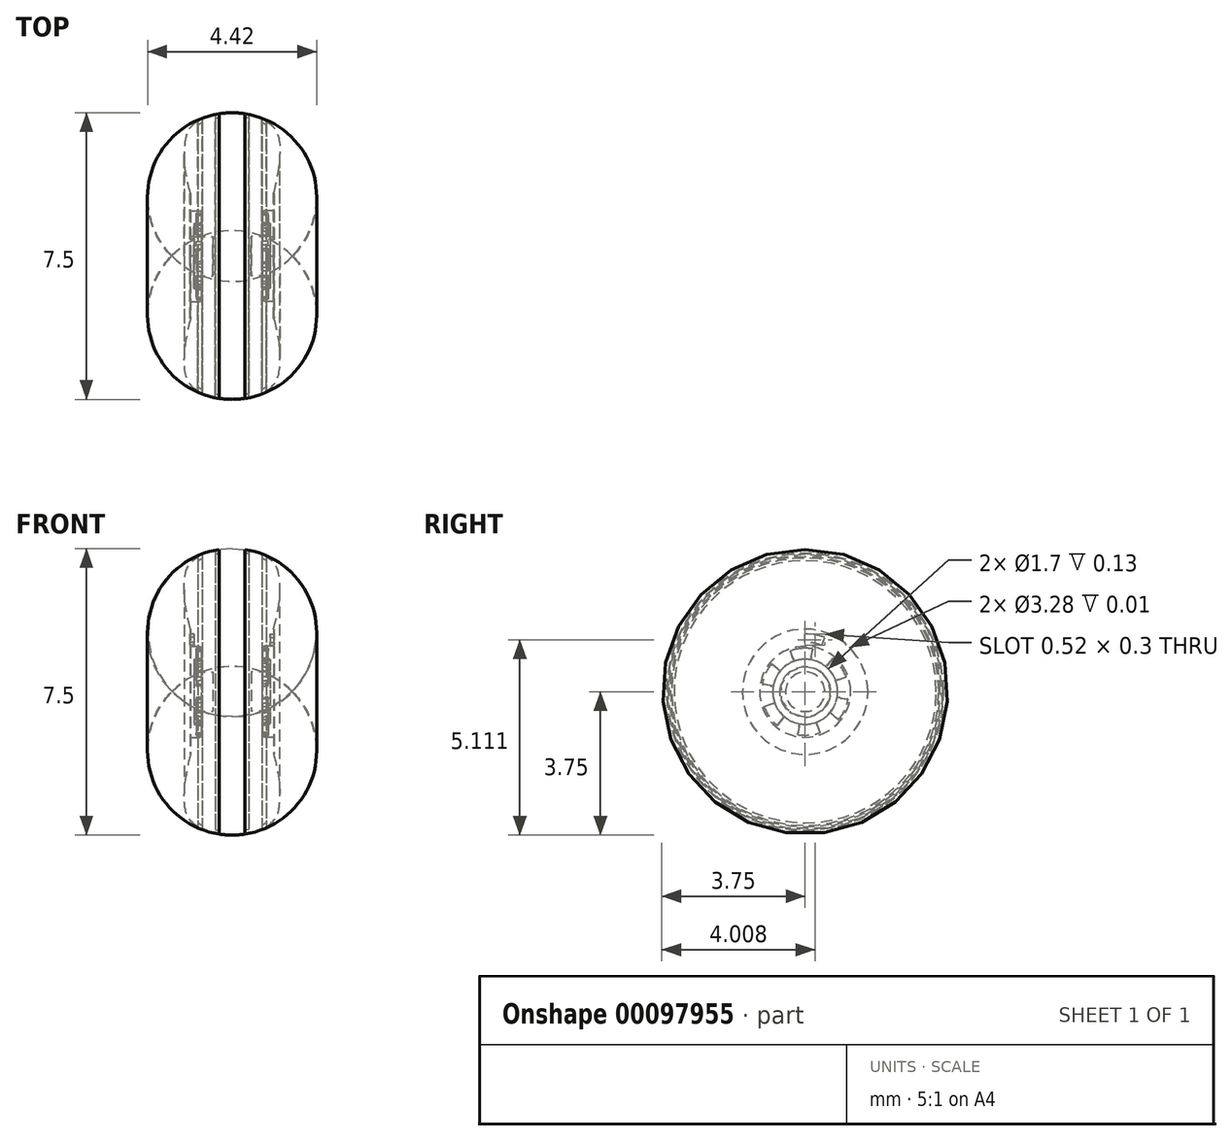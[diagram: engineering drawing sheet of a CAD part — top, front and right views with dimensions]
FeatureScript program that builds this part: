
annotation { "Feature Type Name" : "Feature", "Feature Type Description" : "" }
export const myFeature = defineFeature(function(context is Context, id is Id, definition is map)
    precondition{}
    {
        {
            var Q0;
            Q0=qCreatedBy(makeId("Front.planeOp"),FACE);
            var sketch = newSketch(context, id + "F0", { "sketchPlane" : qUnion([Q0])});
            skLineSegment(sketch, "E0.top", {"start": v(0.87, 0.85) * mm, "end": v(1, 0.85) * mm});
            skLineSegment(sketch, "E0.right", {"start": v(1, 0.51) * mm, "end": v(1, 0.85) * mm});
            skLineSegment(sketch, "E1", {"start": v(0.8, 0.93) * mm, "end": v(0.8, 1.1) * mm});
            skLineSegment(sketch, "E2", {"start": v(0.87, 1.19) * mm, "end": v(1.1, 1.19) * mm});
            skLineSegment(sketch, "E3", {"start": v(1.1, 1.59) * mm, "end": v(1.1, 1.64) * mm});
            skLineSegment(sketch, "E4", {"start": v(1.12, 1.64) * mm, "end": v(1.09, 1.64) * mm});
            skPoint(sketch, "E5.orphan", {"position": v(0, 1.19) * mm});
            skPoint(sketch, "E6.visualSharp", {"position": v(1.1, 1.19) * mm});
            skPoint(sketch, "E7.visualSharp", {"position": v(0.8, 1.19) * mm});
            skArc(sketch, "E7.filletArc", {"start": v(0.87, 1.19) * mm, "mid": v(0.81, 1.17) * mm, "end": v(0.8, 1.1) * mm});
            skArc(sketch, "E8.filletArc", {"start": v(0.8, 0.93) * mm, "mid": v(0.81, 0.87) * mm, "end": v(0.87, 0.85) * mm});
            skPoint(sketch, "E9.visualSharp", {"position": v(1.17, 1.64) * mm});
            skArc(sketch, "E9.filletArc", {"start": v(1.17, 1.59) * mm, "mid": v(1.16, 1.63) * mm, "end": v(1.12, 1.64) * mm});
            skLineSegment(sketch, "E10", {"start": v(-0.76, 3.75) * mm, "end": v(0, 3.75) * mm, "construction": true});
            skLineSegment(sketch, "E11", {"start": v(1.25, 3.84) * mm, "end": v(1.25, 0.98) * mm, "construction": true});
            skLineSegment(sketch, "E12", {"start": v(0, 3.75) * mm, "end": v(1.72, 3.75) * mm, "construction": true});
            skLineSegment(sketch, "E13", {"start": v(1.17, 1.59) * mm, "end": v(1.1, 1.59) * mm});
            skLineSegment(sketch, "E14", {"start": v(1.25, 1.19) * mm, "end": v(1.27, 1.19) * mm});
            skLineSegment(sketch, "E15", {"start": v(1.1, 1.19) * mm, "end": v(1.1, 1.64) * mm});
            skPoint(sketch, "E16.orphan", {"position": v(0, 0.73) * mm});
            skLineSegment(sketch, "E17", {"start": v(0, 0.73) * mm, "end": v(0, 5.2) * mm, "construction": true});
            skLineSegment(sketch, "E18", {"start": v(0.5, 0.52) * mm, "end": v(1, 0.52) * mm});
            skLineSegment(sketch, "E19", {"start": v(0.57, 0) * mm, "end": v(0.57, -0.77) * mm, "construction": true});
            skLineSegment(sketch, "E20", {"start": v(1.1, 4.64) * mm, "end": v(1.1, 3.06) * mm, "construction": true});
            skLineSegment(sketch, "E21", {"start": v(0.97, 3.34) * mm, "end": v(1.1, 3.34) * mm, "construction": true});
            skFitSpline(sketch, "E22", {"points": [v(1.09, 1.64) * mm, v(1.25, 2.8) * mm, v(1.1, 3.34) * mm, v(0, 3.75) * mm], "startDerivative": vector(1.3, 5.18) * mm, "endDerivative": vector(-4.24, 0) * mm});
            skPoint(sketch, "E23", {"position": v(1.25, 2.41) * mm});
            skLineSegment(sketch, "E24", {"start": v(0.34, 3.93) * mm, "end": v(0.34, 3.62) * mm, "construction": true});
            skLineSegment(sketch, "E25", {"start": v(0.44, 3.93) * mm, "end": v(0.44, 3.6) * mm, "construction": true});
            skLineSegment(sketch, "E26", {"start": v(0.78, 3.93) * mm, "end": v(0.78, 3.5) * mm, "construction": true});
            skLineSegment(sketch, "E27", {"start": v(0.9, 3.95) * mm, "end": v(0.9, 3.43) * mm, "construction": true});
            skLineSegment(sketch, "E28", {"start": v(0.34, 3.62) * mm, "end": v(0.44, 3.6) * mm});
            skLineSegment(sketch, "E29", {"start": v(0.78, 3.5) * mm, "end": v(0.9, 3.43) * mm});
            skLineSegment(sketch, "E30", {"start": v(0.34, 3.72) * mm, "end": v(0.34, 3.62) * mm});
            skLineSegment(sketch, "E31", {"start": v(0.44, 3.6) * mm, "end": v(0.44, 3.7) * mm});
            skLineSegment(sketch, "E32", {"start": v(0.78, 3.5) * mm, "end": v(0.78, 3.6) * mm});
            skLineSegment(sketch, "E33", {"start": v(0.9, 3.43) * mm, "end": v(0.9, 3.53) * mm});
            skLineSegment(sketch, "E34", {"start": v(0, 0.52) * mm, "end": v(0, 3.75) * mm});
            skLineSegment(sketch, "E35", {"start": v(0, 0) * mm, "end": v(2.08, 0) * mm, "construction": true});
            skLineSegment(sketch, "E36", {"start": v(0, 0) * mm, "end": v(0, 5.56) * mm, "construction": true});
            skLineSegment(sketch, "E37", {"start": v(0, 0.52) * mm, "end": v(0, 0) * mm});
            skLineSegment(sketch, "E38", {"start": v(0, 0) * mm, "end": v(0.5, 0) * mm});
            skLineSegment(sketch, "E39", {"start": v(0.5, 0) * mm, "end": v(0.5, 0.52) * mm});
            skSolve(sketch);
        }
        {
            var Q0;
            Q0=makeQuery(id+"F0.imprint","IMPRINT",FACE,{"disambiguationData":[TD([[makeQuery(id+"F0.imprint","IMPRINT",EDGE,{"derivedFrom":sQuery(id+"F0.wireOp",EDGE,"E0.top")}),-1.0]])]});
            var Q1;
            Q1=sQuery(id+"F0.wireOp",EDGE,"8bb111fc-4642-4fca-a44e-8b574824e9490.MirrorCS");
            var Q2;
            Q2=sQuery(id+"F0.wireOp",EDGE,"5d76dffb-9663-4801-85ba-127905f750e50.MirrorCS");
            var Q3;
            Q3=sQuery(id+"F0.wireOp",EDGE,"d13460d5-a523-4224-9297-77c6a2cba0c50.MirrorCS");
            var Q4;
            Q4=sQuery(id+"F0.wireOp",EDGE,"c0737af9-8dda-4185-ab45-cae04200aa6d0.MirrorCS");
            var Q5;
            Q5=sQuery(id+"F0.wireOp",EDGE,"E35");
            revolve(context, id + "F1", {"entities" : qUnion([Q0]), "surfaceEntities" : qUnion([Q1, Q2, Q3, Q4]), "axis" : qUnion([Q5]), "revolveType" : RevolveType.FULL});
        }
        {
            var Q0;
            Q0=qCreatedBy(makeId("Front.planeOp"),FACE);
            var sketch = newSketch(context, id + "F2", { "sketchPlane" : qUnion([Q0])});
            skLineSegment(sketch, "E40.bottom", {"start": v(1, 1.51) * mm, "end": v(1.2, 1.51) * mm});
            skLineSegment(sketch, "E40.top", {"start": v(1, 1.29) * mm, "end": v(1.2, 1.29) * mm});
            skLineSegment(sketch, "E40.left", {"start": v(1, 1.51) * mm, "end": v(1, 1.29) * mm});
            skLineSegment(sketch, "E40.right", {"start": v(1.2, 1.51) * mm, "end": v(1.2, 1.29) * mm});
            skLineSegment(sketch, "E41", {"start": v(0, 0) * mm, "end": v(2.72, 0) * mm, "construction": true});
            skSolve(sketch);
        }
        {
            var Q0;
            Q0=qSketchRegion(id+"F2",true);
            var Q1;
            Q1=sQuery(id+"F2.wireOp",EDGE,"E41");
            revolve(context, id + "F3", {"operationType" : NewBodyOperationType.REMOVE, "entities" : qUnion([Q0]), "axis" : qUnion([Q1]), "revolveType" : RevolveType.ONE_DIRECTION, "oppositeDirection" : true, "angle" : 20 * degree});
        }
        {
            var Q0;
            Q0=makeQuery(id+"F1.opRevolve","SWEPT_FACE",FACE,{"disambiguationData":[OSD([sQuery(id+"F0.wireOp",EDGE,"E1")])]});
            var sketch = newSketch(context, id + "F4", { "sketchPlane" : qUnion([Q0])});
            skLineSegment(sketch, "E42", {"start": v(-0.27, 0.74) * mm, "end": v(-0.39, 1.07) * mm});
            skArc(sketch, "E43", {"start": v(-0.39, 1.07) * mm, "mid": v(-0.1, 1.13) * mm, "end": v(0.2, 1.12) * mm});
            skLineSegment(sketch, "E44", {"start": v(0.14, 0.78) * mm, "end": v(0.2, 1.12) * mm});
            skArc(sketch, "E45", {"start": v(-0.27, 0.74) * mm, "mid": v(-0.07, 0.79) * mm, "end": v(0.14, 0.78) * mm});
            skLineSegment(sketch, "E46.1.0", {"start": v(-0.78, 0.14) * mm, "end": v(-1.12, 0.2) * mm});
            skArc(sketch, "E46.1.1", {"start": v(-1.12, 0.2) * mm, "mid": v(-1.03, 0.48) * mm, "end": v(-0.87, 0.73) * mm});
            skLineSegment(sketch, "E46.1.2", {"start": v(-0.6, 0.5) * mm, "end": v(-0.87, 0.73) * mm});
            skArc(sketch, "E46.1.3", {"start": v(-0.78, 0.14) * mm, "mid": v(-0.71, 0.33) * mm, "end": v(-0.6, 0.5) * mm});
            skLineSegment(sketch, "E46.2.0", {"start": v(-0.5, -0.6) * mm, "end": v(-0.73, -0.87) * mm});
            skArc(sketch, "E46.2.1", {"start": v(-0.73, -0.87) * mm, "mid": v(-0.93, -0.65) * mm, "end": v(-1.07, -0.39) * mm});
            skLineSegment(sketch, "E46.2.2", {"start": v(-0.74, -0.27) * mm, "end": v(-1.07, -0.39) * mm});
            skArc(sketch, "E46.2.3", {"start": v(-0.5, -0.6) * mm, "mid": v(-0.65, -0.45) * mm, "end": v(-0.74, -0.27) * mm});
            skLineSegment(sketch, "E47.1.3.0", {"start": v(0.27, -0.74) * mm, "end": v(0.39, -1.07) * mm});
            skArc(sketch, "E47.3.3.0", {"start": v(0.39, -1.07) * mm, "mid": v(0.1, -1.13) * mm, "end": v(-0.2, -1.12) * mm});
            skLineSegment(sketch, "E47.7.3.0", {"start": v(-0.14, -0.78) * mm, "end": v(-0.2, -1.12) * mm});
            skArc(sketch, "E47.10.3.0", {"start": v(0.27, -0.74) * mm, "mid": v(0.07, -0.79) * mm, "end": v(-0.14, -0.78) * mm});
            skLineSegment(sketch, "E47.1.4.0", {"start": v(0.78, -0.14) * mm, "end": v(1.12, -0.2) * mm});
            skArc(sketch, "E47.3.4.0", {"start": v(1.12, -0.2) * mm, "mid": v(1.03, -0.48) * mm, "end": v(0.87, -0.73) * mm});
            skLineSegment(sketch, "E47.7.4.0", {"start": v(0.6, -0.5) * mm, "end": v(0.87, -0.73) * mm});
            skArc(sketch, "E47.10.4.0", {"start": v(0.78, -0.14) * mm, "mid": v(0.71, -0.33) * mm, "end": v(0.6, -0.5) * mm});
            skLineSegment(sketch, "E47.1.5.0", {"start": v(0.5, 0.6) * mm, "end": v(0.73, 0.87) * mm});
            skArc(sketch, "E47.3.5.0", {"start": v(0.73, 0.87) * mm, "mid": v(0.93, 0.65) * mm, "end": v(1.07, 0.39) * mm});
            skLineSegment(sketch, "E47.7.5.0", {"start": v(0.74, 0.27) * mm, "end": v(1.07, 0.39) * mm});
            skArc(sketch, "E47.10.5.0", {"start": v(0.5, 0.6) * mm, "mid": v(0.65, 0.45) * mm, "end": v(0.74, 0.27) * mm});
            skSolve(sketch);
        }
        {
            var Q0;
            Q0 = qSketchRegion(id + "F4", true);
            extrude(context, id + "F5", {"entities" : qUnion([Q0]), "operationType" : NewBodyOperationType.ADD, "depth" : .15 * mm});
        }
        {
            var Q0;
            Q0=makeQuery(id+"F1.opRevolve","SWEPT_BODY",BODY,{"disambiguationData":[OSD([sQuery(id+"F0.wireOp",EDGE,"E0.top"),sQuery(id+"F0.wireOp",EDGE,"E0.right"),sQuery(id+"F0.wireOp",EDGE,"E1"),sQuery(id+"F0.wireOp",EDGE,"E2"),sQuery(id+"F0.wireOp",EDGE,"E4"),sQuery(id+"F0.wireOp",EDGE,"E7.filletArc"),sQuery(id+"F0.wireOp",EDGE,"E8.filletArc"),sQuery(id+"F0.wireOp",EDGE,"E15"),sQuery(id+"F0.wireOp",EDGE,"E18"),sQuery(id+"F0.wireOp",EDGE,"E22"),sQuery(id+"F0.wireOp",EDGE,"E28"),sQuery(id+"F0.wireOp",EDGE,"E29"),sQuery(id+"F0.wireOp",EDGE,"E30"),sQuery(id+"F0.wireOp",EDGE,"E31"),sQuery(id+"F0.wireOp",EDGE,"E32"),sQuery(id+"F0.wireOp",EDGE,"E33"),sQuery(id+"F0.wireOp",EDGE,"E22"),sQuery(id+"F0.wireOp",EDGE,"E22"),sQuery(id+"F0.wireOp",EDGE,"E34")])]});
            var Q1;
            Q1=makeQuery(id+"F1.opRevolve","SWEPT_FACE",FACE,{"disambiguationData":[OSD([sQuery(id+"F0.wireOp",EDGE,"E34")])]});
            mirror(context, id + "F6", {"operationType" : NewBodyOperationType.ADD, "entities" : qUnion([Q0]), "mirrorPlane" : qUnion([Q1])});
        }
    });
